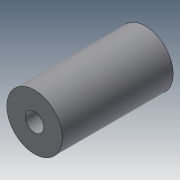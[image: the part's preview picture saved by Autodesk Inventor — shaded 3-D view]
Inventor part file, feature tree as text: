
AUTODESK INVENTOR PART (.ipt)
format: ipt  version: 2018.3 (Build 223284000, 284)  size: 98,816 bytes
history: native  units: in
note: dims shown in document units (in); Inventor stores cm internally (conversion verified against a paired STEP export)
features: extrude x1
ambient origin geometry x8: Origin, YZ Plane, XZ Plane, XY Plane, X Axis, Y Axis, Z Axis, Center Point
bodies: Solid1 (feature_tree)
feature tree (1):
  extrude  "Extrude1"  [1 undecoded]
note: 1 required parameter value undecoded (feature->parameter linkage not recoverable at this tier; creation-order binding heuristic only, values carry confidence <= 0.55)
